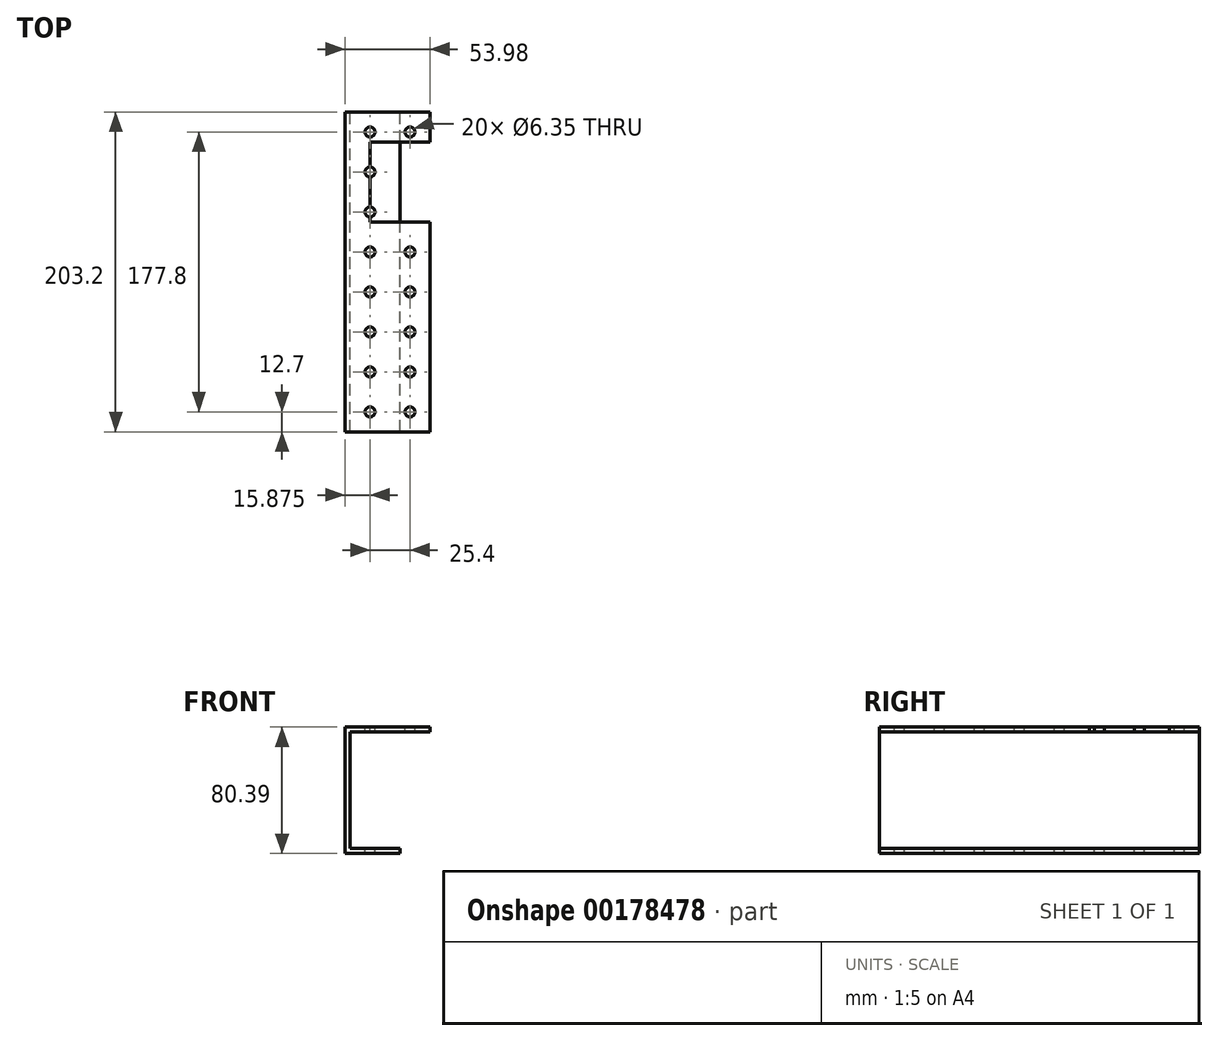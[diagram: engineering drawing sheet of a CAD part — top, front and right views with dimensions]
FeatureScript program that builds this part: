
annotation { "Feature Type Name" : "Feature", "Feature Type Description" : "" }
export const myFeature = defineFeature(function(context is Context, id is Id, definition is map)
    precondition{}
    {
        {
            var Q0;
            Q0=qCreatedBy(makeId("Front.planeOp"),FACE);
            var sketch = newSketch(context, id + "F0", { "sketchPlane" : qUnion([Q0])});
            skLineSegment(sketch, "E0", {"start": v(0, 44.52) * mm, "end": v(0, -35.87) * mm});
            skLineSegment(sketch, "E1", {"start": v(0, 44.52) * mm, "end": v(53.98, 44.52) * mm});
            skLineSegment(sketch, "E2", {"start": v(0, -35.87) * mm, "end": v(34.93, -35.87) * mm});
            skLineSegment(sketch, "E3", {"start": v(34.93, -35.87) * mm, "end": v(34.93, -32.7) * mm});
            skLineSegment(sketch, "E4", {"start": v(34.93, -32.7) * mm, "end": v(3.18, -32.7) * mm});
            skLineSegment(sketch, "E5", {"start": v(3.18, -32.7) * mm, "end": v(3.18, 41.34) * mm});
            skLineSegment(sketch, "E6", {"start": v(3.18, 41.34) * mm, "end": v(53.98, 41.34) * mm});
            skLineSegment(sketch, "E7", {"start": v(53.98, 41.34) * mm, "end": v(53.98, 44.52) * mm});
            skSolve(sketch);
        }
        {
            var Q0;
            Q0=makeQuery(id+"F0.imprint","IMPRINT",FACE,{"disambiguationData":[TD([[makeQuery(id+"F0.imprint","IMPRINT",EDGE,{"derivedFrom":sQuery(id+"F0.wireOp",EDGE,"E0")}),1.0]])]});
            extrude(context, id + "F1", {"entities" : qUnion([Q0]), "depth" : 203.2 * mm});
        }
        {
            var Q0;
            Q0=makeQuery(id+"F1.opExtrude","SWEPT_FACE",FACE,{"disambiguationData":[OSD([sQuery(id+"F0.wireOp",EDGE,"E1")])]});
            var sketch = newSketch(context, id + "F2", { "sketchPlane" : qUnion([Q0])});
            skLineSegment(sketch, "E8.bottom", {"start": v(53.98, -19.05) * mm, "end": v(15.87, -19.05) * mm});
            skLineSegment(sketch, "E8.top", {"start": v(53.98, -69.85) * mm, "end": v(15.88, -69.85) * mm});
            skLineSegment(sketch, "E8.left", {"start": v(53.98, -19.05) * mm, "end": v(53.98, -69.85) * mm});
            skLineSegment(sketch, "E8.right", {"start": v(15.87, -19.05) * mm, "end": v(15.88, -69.85) * mm});
            skLineSegment(sketch, "E9", {"start": v(15.24, -37.47) * mm, "end": v(15.24, -18.42) * mm});
            skLineSegment(sketch, "E10", {"start": v(15.24, -18.42) * mm, "end": v(-22.86, -18.42) * mm});
            skLineSegment(sketch, "E11", {"start": v(-22.86, -18.42) * mm, "end": v(-22.86, 32.38) * mm});
            skLineSegment(sketch, "E12", {"start": v(-22.86, 32.38) * mm, "end": v(15.24, 32.38) * mm});
            skLineSegment(sketch, "E13", {"start": v(15.24, 32.38) * mm, "end": v(15.24, -18.42) * mm});
            skSolve(sketch);
        }
        {
            var Q0;
            {var subQ10=sQuery(id+"F2.wireOp",EDGE,"E8.left");Q0=makeQuery(id+"F2.imprint","IMPRINT",FACE,{"disambiguationData":[TD([[makeQuery(id+"F2.imprint","IMPRINT",EDGE,{"derivedFrom":subQ10}),1.0]])]});}
            extrude(context, id + "F3", {"entities" : qUnion([Q0]), "operationType" : NewBodyOperationType.REMOVE, "oppositeDirection" : true, "depth" : 25.4 * mm});
        }
        {
            var Q0;
            Q0=makeQuery(id+"F1.opExtrude","SWEPT_FACE",FACE,{"disambiguationData":[OSD([sQuery(id+"F0.wireOp",EDGE,"E1")])]});
            var sketch = newSketch(context, id + "F4", { "sketchPlane" : qUnion([Q0])});
            skCircle(sketch, "E14", {"center": v(41.27, -190.5) * mm, "radius": 3.18 * mm});
            skCircle(sketch, "E15.0.1.0", {"center": v(41.27, -165.1) * mm, "radius": 3.18 * mm});
            skCircle(sketch, "E15.0.2.0", {"center": v(41.27, -139.7) * mm, "radius": 3.18 * mm});
            skCircle(sketch, "E15.0.3.0", {"center": v(41.27, -114.3) * mm, "radius": 3.18 * mm});
            skCircle(sketch, "E15.0.4.0", {"center": v(41.27, -88.9) * mm, "radius": 3.18 * mm});
            skCircle(sketch, "E15.0.5.0", {"center": v(41.27, -63.5) * mm, "radius": 3.18 * mm});
            skCircle(sketch, "E15.0.6.0", {"center": v(41.27, -38.1) * mm, "radius": 3.18 * mm});
            skCircle(sketch, "E15.0.7.0", {"center": v(41.27, -12.7) * mm, "radius": 3.18 * mm});
            skCircle(sketch, "E15.1.0.0", {"center": v(15.87, -190.5) * mm, "radius": 3.18 * mm});
            skCircle(sketch, "E15.1.1.0", {"center": v(15.87, -165.1) * mm, "radius": 3.18 * mm});
            skCircle(sketch, "E15.1.2.0", {"center": v(15.87, -139.7) * mm, "radius": 3.18 * mm});
            skCircle(sketch, "E15.1.3.0", {"center": v(15.87, -114.3) * mm, "radius": 3.18 * mm});
            skCircle(sketch, "E15.1.4.0", {"center": v(15.87, -88.9) * mm, "radius": 3.18 * mm});
            skCircle(sketch, "E15.1.5.0", {"center": v(15.87, -63.5) * mm, "radius": 3.18 * mm});
            skCircle(sketch, "E15.1.6.0", {"center": v(15.87, -38.1) * mm, "radius": 3.18 * mm});
            skCircle(sketch, "E15.1.7.0", {"center": v(15.87, -12.7) * mm, "radius": 3.18 * mm});
            skLineSegment(sketch, "E15.direction1", {"start": v(41.27, -190.5) * mm, "end": v(15.87, -190.5) * mm, "construction": true});
            skLineSegment(sketch, "E15.direction2", {"start": v(41.27, -190.5) * mm, "end": v(41.27, -165.1) * mm, "construction": true});
            skSolve(sketch);
        }
        {
            var Q0;
            Q0=qSketchRegion(id+"F4",true);
            extrude(context, id + "F5", {"entities" : qUnion([Q0]), "operationType" : NewBodyOperationType.REMOVE, "oppositeDirection" : true, "depth" : 101.6 * mm});
        }
    });
